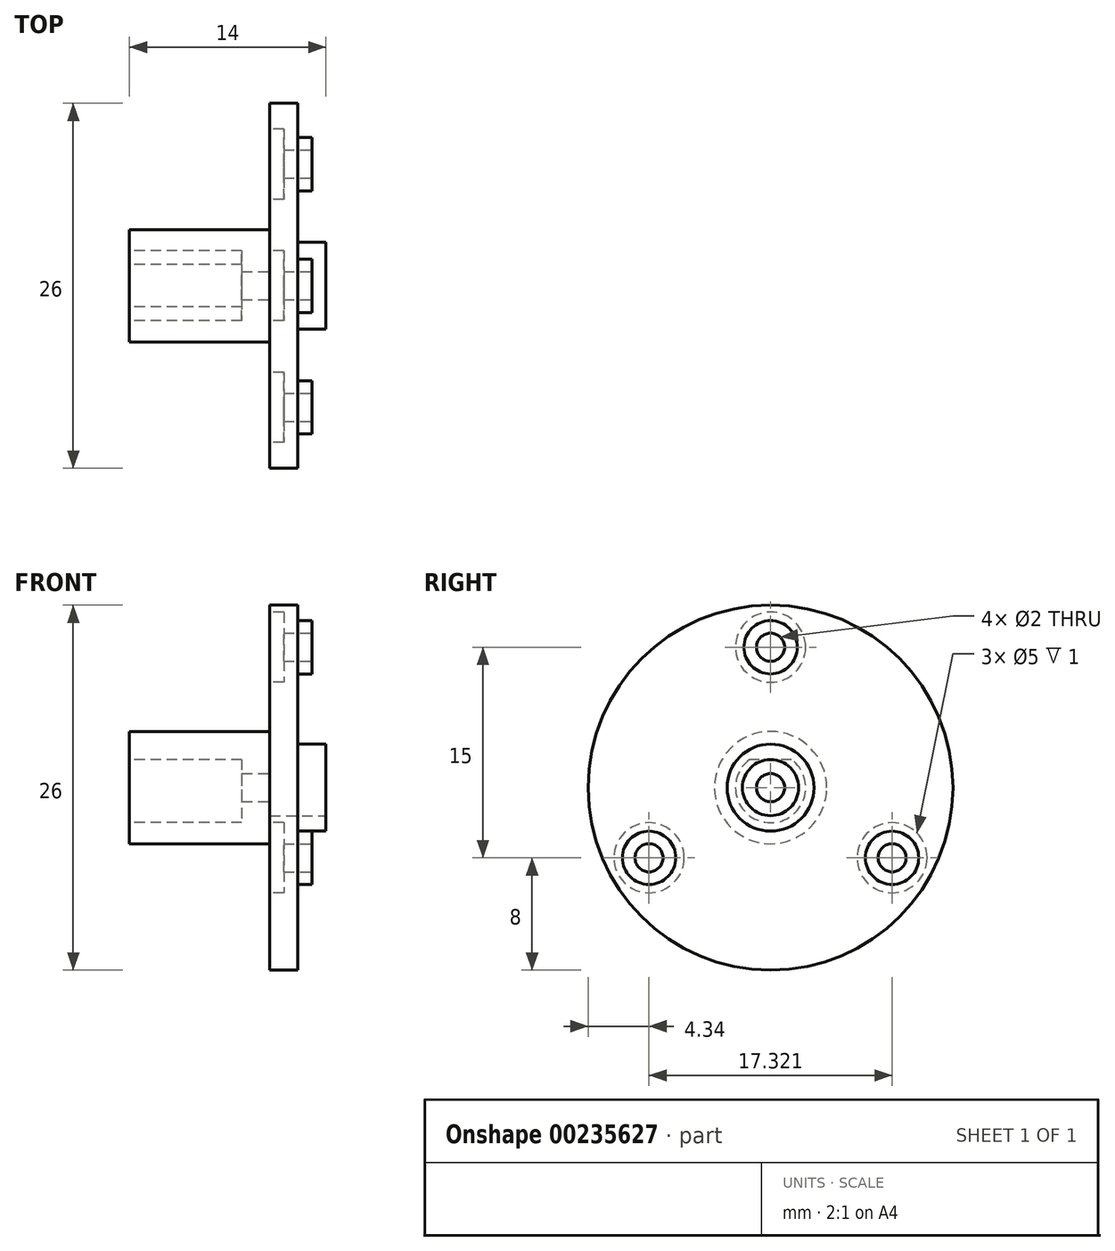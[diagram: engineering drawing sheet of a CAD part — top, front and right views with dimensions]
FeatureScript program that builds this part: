
annotation { "Feature Type Name" : "Feature", "Feature Type Description" : "" }
export const myFeature = defineFeature(function(context is Context, id is Id, definition is map)
    precondition{}
    {
        {
            var Q0;
            Q0=qCreatedBy(makeId("Right.planeOp"),FACE);
            var sketch = newSketch(context, id + "F0", { "sketchPlane" : qUnion([Q0])});
            skCircle(sketch, "E0", {"center": v(0, 0) * mm, "radius": 13 * mm});
            skCircle(sketch, "E1", {"center": v(0, 0) * mm, "radius": 10 * mm, "construction": true});
            skPoint(sketch, "E2", {"position": v(0, 10) * mm});
            skLineSegment(sketch, "E3", {"start": v(0, 0) * mm, "end": v(11.26, -6.5) * mm, "construction": true});
            skLineSegment(sketch, "E4", {"start": v(0, 0) * mm, "end": v(-11.26, -6.5) * mm, "construction": true});
            skPoint(sketch, "E5", {"position": v(8.66, -5) * mm});
            skPoint(sketch, "E6", {"position": v(-8.66, -5) * mm});
            skCircle(sketch, "E7", {"center": v(0, 10) * mm, "radius": 1 * mm});
            skCircle(sketch, "E8", {"center": v(8.66, -5) * mm, "radius": 1 * mm});
            skCircle(sketch, "E9", {"center": v(-8.66, -5) * mm, "radius": 1 * mm});
            skCircle(sketch, "E10", {"center": v(0, 0) * mm, "radius": 2 * mm});
            skSolve(sketch);
        }
        {
            var Q0;
            Q0 = qSketchRegion(id + "F0", true);
            extrude(context, id + "F1", {"entities" : qUnion([Q0]), "oppositeDirection" : true, "depth" : 2 * mm});
        }
        {
            var Q0;
            Q0=makeQuery(id+"F1.opExtrude","CAP_FACE",FACE,{"disambiguationData":[OSD([sQuery(id+"F0.wireOp",EDGE,"E0"),sQuery(id+"F0.wireOp",EDGE,"E7"),sQuery(id+"F0.wireOp",EDGE,"E8"),sQuery(id+"F0.wireOp",EDGE,"E9"),sQuery(id+"F0.wireOp",EDGE,"E10")])],"isStart":true});
            var sketch = newSketch(context, id + "F2", { "sketchPlane" : qUnion([Q0])});
            skCircle(sketch, "E11", {"center": v(0, 10) * mm, "radius": 1.9 * mm});
            skCircle(sketch, "E12", {"center": v(8.66, -5) * mm, "radius": 1.9 * mm});
            skCircle(sketch, "E13", {"center": v(-8.66, -5) * mm, "radius": 1.9 * mm});
            skCircle(sketch, "E14", {"center": v(0, 10) * mm, "radius": 1 * mm});
            skCircle(sketch, "E15", {"center": v(8.66, -5) * mm, "radius": 1 * mm});
            skCircle(sketch, "E16", {"center": v(-8.66, -5) * mm, "radius": 1 * mm});
            skSolve(sketch);
        }
        {
            var Q0;
            Q0=makeQuery(id+"F1.opExtrude","CAP_FACE",FACE,{"disambiguationData":[OSD([sQuery(id+"F0.wireOp",EDGE,"E0"),sQuery(id+"F0.wireOp",EDGE,"E7"),sQuery(id+"F0.wireOp",EDGE,"E8"),sQuery(id+"F0.wireOp",EDGE,"E9"),sQuery(id+"F0.wireOp",EDGE,"E10")])],"isStart":true});
            var sketch = newSketch(context, id + "F3", { "sketchPlane" : qUnion([Q0])});
            skCircle(sketch, "E17", {"center": v(0, 0) * mm, "radius": 3.1 * mm});
            skCircle(sketch, "E18", {"center": v(0, 0) * mm, "radius": 2 * mm});
            skSolve(sketch);
        }
        {
            var Q0;
            Q0=makeQuery(id+"F1.opExtrude","CAP_FACE",FACE,{"disambiguationData":[OSD([sQuery(id+"F0.wireOp",EDGE,"E0"),sQuery(id+"F0.wireOp",EDGE,"E7"),sQuery(id+"F0.wireOp",EDGE,"E8"),sQuery(id+"F0.wireOp",EDGE,"E9"),sQuery(id+"F0.wireOp",EDGE,"E10")])],"isStart":false});
            var sketch = newSketch(context, id + "F4", { "sketchPlane" : qUnion([Q0])});
            skCircle(sketch, "E19", {"center": v(0, 0) * mm, "radius": 4 * mm});
            skCircle(sketch, "E20", {"center": v(0, 0) * mm, "radius": 1 * mm});
            skSolve(sketch);
        }
        {
            var Q0;
            Q0 = qSketchRegion(id + "F4", true);
            extrude(context, id + "F5", {"entities" : qUnion([Q0]), "operationType" : NewBodyOperationType.ADD, "depth" : 10 * mm});
        }
        {
            var Q0;
            Q0=makeQuery(id+"F1.opExtrude","CAP_FACE",FACE,{"disambiguationData":[OSD([sQuery(id+"F0.wireOp",EDGE,"E0"),sQuery(id+"F0.wireOp",EDGE,"E7"),sQuery(id+"F0.wireOp",EDGE,"E8"),sQuery(id+"F0.wireOp",EDGE,"E9"),sQuery(id+"F0.wireOp",EDGE,"E10")])],"isStart":false});
            var sketch = newSketch(context, id + "F6", { "sketchPlane" : qUnion([Q0])});
            skCircle(sketch, "E21", {"center": v(0, 10) * mm, "radius": 2.5 * mm});
            skCircle(sketch, "E22", {"center": v(8.66, -5) * mm, "radius": 2.5 * mm});
            skCircle(sketch, "E23", {"center": v(-8.66, -5) * mm, "radius": 2.5 * mm});
            skCircle(sketch, "E24", {"center": v(0, 10) * mm, "radius": 1 * mm});
            skCircle(sketch, "E25", {"center": v(8.66, -5) * mm, "radius": 1 * mm});
            skCircle(sketch, "E26", {"center": v(-8.66, -5) * mm, "radius": 1 * mm});
            skSolve(sketch);
        }
        {
            var Q0;
            Q0 = qSketchRegion(id + "F6", true);
            extrude(context, id + "F7", {"entities" : qUnion([Q0]), "operationType" : NewBodyOperationType.REMOVE, "oppositeDirection" : true, "depth" : 1 * mm});
        }
        {
            var Q0;
            Q0=makeQuery(id+"F5.opExtrude","CAP_FACE",FACE,{"disambiguationData":[OSD([sQuery(id+"F4.wireOp",EDGE,"E19"),sQuery(id+"F4.wireOp",EDGE,"E20")])],"isStart":false});
            var sketch = newSketch(context, id + "F8", { "sketchPlane" : qUnion([Q0])});
            skCircle(sketch, "E27", {"center": v(0, 0) * mm, "radius": 2.5 * mm});
            skLineSegment(sketch, "E28.bottom", {"start": v(-2, 2) * mm, "end": v(2, 2) * mm});
            skLineSegment(sketch, "E28.top", {"start": v(-2, 3) * mm, "end": v(2, 3) * mm});
            skLineSegment(sketch, "E28.left", {"start": v(-2, 2) * mm, "end": v(-2, 3) * mm});
            skLineSegment(sketch, "E28.right", {"start": v(2, 2) * mm, "end": v(2, 3) * mm});
            skPoint(sketch, "E28.middle", {"position": v(0, 2.5) * mm});
            skSolve(sketch);
        }
        {
            var Q0;
            Q0=makeQuery(id+"F8.imprint","IMPRINT",FACE,{"disambiguationData":[TD([[makeQuery(id+"F8.imprint","IMPRINT",EDGE,{"derivedFrom":makeQuery(id+"F5.opExtrude","CAP_EDGE",EDGE,{"disambiguationData":[OSD([sQuery(id+"F4.wireOp",EDGE,"E20")])],"isStart":false})}),1.0]])]});
            var Q1;
            Q1=makeQuery(id+"F8.imprint","IMPRINT",FACE,{"disambiguationData":[TD([[makeQuery(id+"F8.imprint","IMPRINT",EDGE,{"derivedFrom":makeQuery(id+"F5.opExtrude","CAP_EDGE",EDGE,{"disambiguationData":[OSD([sQuery(id+"F4.wireOp",EDGE,"E20")])],"isStart":false})}),-1.0]])]});
            extrude(context, id + "F9", {"entities" : qUnion([Q0, Q1]), "operationType" : NewBodyOperationType.REMOVE, "oppositeDirection" : true, "depth" : 8 * mm});
        }
        {
            var Q0;
            Q0 = qSketchRegion(id + "F2", true);
            extrude(context, id + "F10", {"entities" : qUnion([Q0]), "operationType" : NewBodyOperationType.ADD, "depth" : 1 * mm});
        }
        {
            var Q0;
            Q0 = qSketchRegion(id + "F3", true);
            extrude(context, id + "F11", {"entities" : qUnion([Q0]), "operationType" : NewBodyOperationType.ADD, "depth" : 2 * mm});
        }
    });
